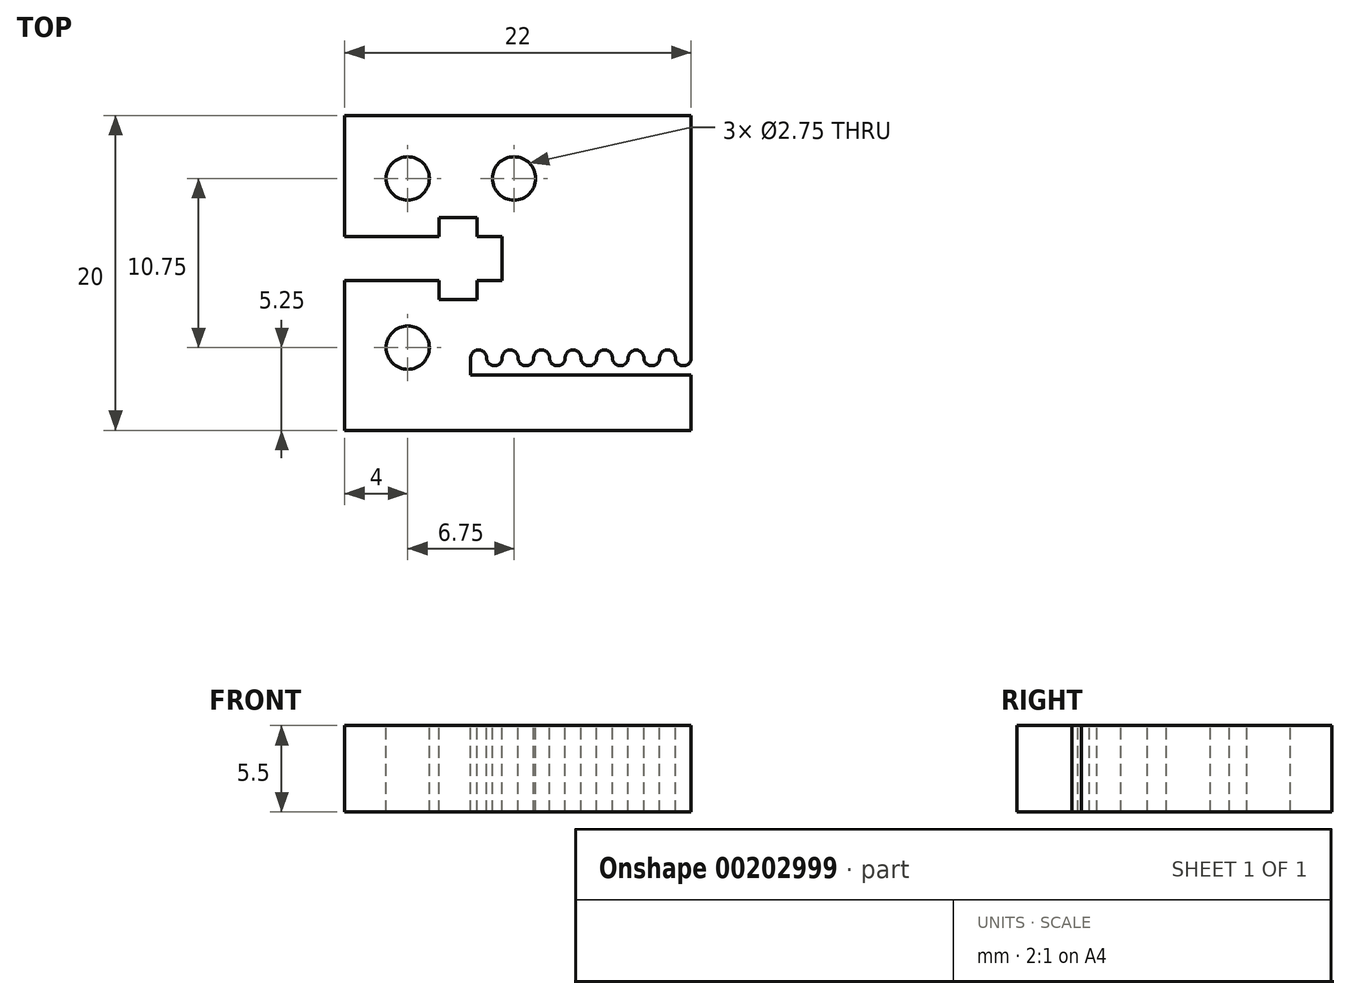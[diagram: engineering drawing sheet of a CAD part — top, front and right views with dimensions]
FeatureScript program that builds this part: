
annotation { "Feature Type Name" : "Feature", "Feature Type Description" : "" }
export const myFeature = defineFeature(function(context is Context, id is Id, definition is map)
    precondition{}
    {
        {
            var Q0;
            Q0=qCreatedBy(makeId("Top.planeOp"),FACE);
            var sketch = newSketch(context, id + "F0", { "sketchPlane" : qUnion([Q0])});
            skLineSegment(sketch, "E0.bottom", {"start": v(11, -10) * mm, "end": v(-11, -10) * mm});
            skLineSegment(sketch, "E0.top", {"start": v(11, 10) * mm, "end": v(-11, 10) * mm});
            skLineSegment(sketch, "E0.left", {"start": v(11, -10) * mm, "end": v(11, 10) * mm});
            skLineSegment(sketch, "E0.right", {"start": v(-11, -10) * mm, "end": v(-11, 10) * mm});
            skPoint(sketch, "E0.middle", {"position": v(0, 0) * mm});
            skSolve(sketch);
        }
        {
            var Q0;
            Q0 = qSketchRegion(id + "F0", true);
            extrude(context, id + "F1", {"entities" : qUnion([Q0]), "depth" : 5.5 * mm});
        }
        {
            var Q0;
            Q0=makeQuery(id+"F1.opExtrude","CAP_FACE",FACE,{"disambiguationData":[OSD([sQuery(id+"F0.wireOp",EDGE,"E0.bottom"),sQuery(id+"F0.wireOp",EDGE,"E0.top"),sQuery(id+"F0.wireOp",EDGE,"E0.left"),sQuery(id+"F0.wireOp",EDGE,"E0.right")])],"isStart":false});
            var sketch = newSketch(context, id + "F2", { "sketchPlane" : qUnion([Q0])});
            skCircle(sketch, "E1", {"center": v(-0.25, 6) * mm, "radius": 1.38 * mm});
            skCircle(sketch, "E2", {"center": v(-7, 6) * mm, "radius": 1.38 * mm});
            skCircle(sketch, "E3", {"center": v(-7, -4.75) * mm, "radius": 1.38 * mm});
            skSolve(sketch);
        }
        {
            var Q0;
            Q0 = qSketchRegion(id + "F2", true);
            extrude(context, id + "F3", {"entities" : qUnion([Q0]), "operationType" : NewBodyOperationType.REMOVE, "oppositeDirection" : true, "depth" : 25 * mm});
        }
        {
            var Q0;
            Q0=makeQuery(id+"F1.opExtrude","CAP_FACE",FACE,{"disambiguationData":[OSD([sQuery(id+"F0.wireOp",EDGE,"E0.bottom"),sQuery(id+"F0.wireOp",EDGE,"E0.top"),sQuery(id+"F0.wireOp",EDGE,"E0.left"),sQuery(id+"F0.wireOp",EDGE,"E0.right")])],"isStart":false});
            var sketch = newSketch(context, id + "F4", { "sketchPlane" : qUnion([Q0])});
            skLineSegment(sketch, "E4.bottom", {"start": v(-11, 2.3) * mm, "end": v(-1, 2.3) * mm});
            skLineSegment(sketch, "E4.top", {"start": v(-11, -0.5) * mm, "end": v(-1, -0.5) * mm});
            skLineSegment(sketch, "E4.left", {"start": v(-11, 2.3) * mm, "end": v(-11, -0.5) * mm});
            skLineSegment(sketch, "E4.right", {"start": v(-1, 2.3) * mm, "end": v(-1, -0.5) * mm});
            skLineSegment(sketch, "E5.bottom", {"start": v(-2.6, -1.7) * mm, "end": v(-5, -1.7) * mm});
            skLineSegment(sketch, "E5.top", {"start": v(-2.6, 3.5) * mm, "end": v(-5, 3.5) * mm});
            skLineSegment(sketch, "E5.left", {"start": v(-2.6, -1.7) * mm, "end": v(-2.6, 3.5) * mm});
            skLineSegment(sketch, "E5.right", {"start": v(-5, -1.7) * mm, "end": v(-5, 3.5) * mm});
            skSolve(sketch);
        }
        {
            var Q0;
            Q0 = qSketchRegion(id + "F4", true);
            extrude(context, id + "F5", {"entities" : qUnion([Q0]), "operationType" : NewBodyOperationType.REMOVE, "oppositeDirection" : true, "depth" : 25 * mm});
        }
        {
            var Q0;
            Q0=makeQuery(id+"F1.opExtrude","CAP_FACE",FACE,{"disambiguationData":[OSD([sQuery(id+"F0.wireOp",EDGE,"E0.bottom"),sQuery(id+"F0.wireOp",EDGE,"E0.top"),sQuery(id+"F0.wireOp",EDGE,"E0.left"),sQuery(id+"F0.wireOp",EDGE,"E0.right")])],"isStart":false});
            var sketch = newSketch(context, id + "F6", { "sketchPlane" : qUnion([Q0])});
            skLineSegment(sketch, "E6.bottom", {"start": v(11, -6.5) * mm, "end": v(-3, -6.5) * mm});
            skLineSegment(sketch, "E6.right", {"start": v(-3, -6.5) * mm, "end": v(-3, -5.4) * mm});
            skArc(sketch, "E7", {"start": v(-2, -5.4) * mm, "mid": v(-2.5, -4.9) * mm, "end": v(-3, -5.4) * mm});
            skArc(sketch, "E8", {"start": v(-2, -5.4) * mm, "mid": v(-1.5, -5.9) * mm, "end": v(-1, -5.4) * mm});
            skArc(sketch, "E9", {"start": v(0, -5.4) * mm, "mid": v(-0.5, -4.9) * mm, "end": v(-1, -5.4) * mm});
            skArc(sketch, "E10", {"start": v(0, -5.4) * mm, "mid": v(0.5, -5.9) * mm, "end": v(1, -5.4) * mm});
            skArc(sketch, "E11", {"start": v(1, -5.4) * mm, "mid": v(1.5, -4.9) * mm, "end": v(2, -5.4) * mm});
            skArc(sketch, "E12", {"start": v(2, -5.4) * mm, "mid": v(2.5, -5.9) * mm, "end": v(3, -5.4) * mm});
            skArc(sketch, "E13", {"start": v(4, -5.4) * mm, "mid": v(3.5, -4.9) * mm, "end": v(3, -5.4) * mm});
            skArc(sketch, "E14", {"start": v(4, -5.4) * mm, "mid": v(4.5, -5.9) * mm, "end": v(5, -5.4) * mm});
            skArc(sketch, "E15", {"start": v(6, -5.4) * mm, "mid": v(5.5, -4.9) * mm, "end": v(5, -5.4) * mm});
            skArc(sketch, "E16", {"start": v(6, -5.4) * mm, "mid": v(6.5, -5.9) * mm, "end": v(7, -5.4) * mm});
            skArc(sketch, "E17", {"start": v(8, -5.4) * mm, "mid": v(7.5, -4.9) * mm, "end": v(7, -5.4) * mm});
            skArc(sketch, "E18", {"start": v(8, -5.4) * mm, "mid": v(8.5, -5.9) * mm, "end": v(9, -5.4) * mm});
            skArc(sketch, "E19", {"start": v(10, -5.4) * mm, "mid": v(9.5, -4.9) * mm, "end": v(9, -5.4) * mm});
            skArc(sketch, "E20", {"start": v(10, -5.4) * mm, "mid": v(10.5, -5.9) * mm, "end": v(11, -5.4) * mm});
            skLineSegment(sketch, "E21", {"start": v(11, -5.4) * mm, "end": v(11, -6.5) * mm});
            skSolve(sketch);
        }
        {
            var Q0;
            Q0 = qSketchRegion(id + "F6", true);
            extrude(context, id + "F7", {"entities" : qUnion([Q0]), "operationType" : NewBodyOperationType.REMOVE, "oppositeDirection" : true, "depth" : 25 * mm});
        }
    });
